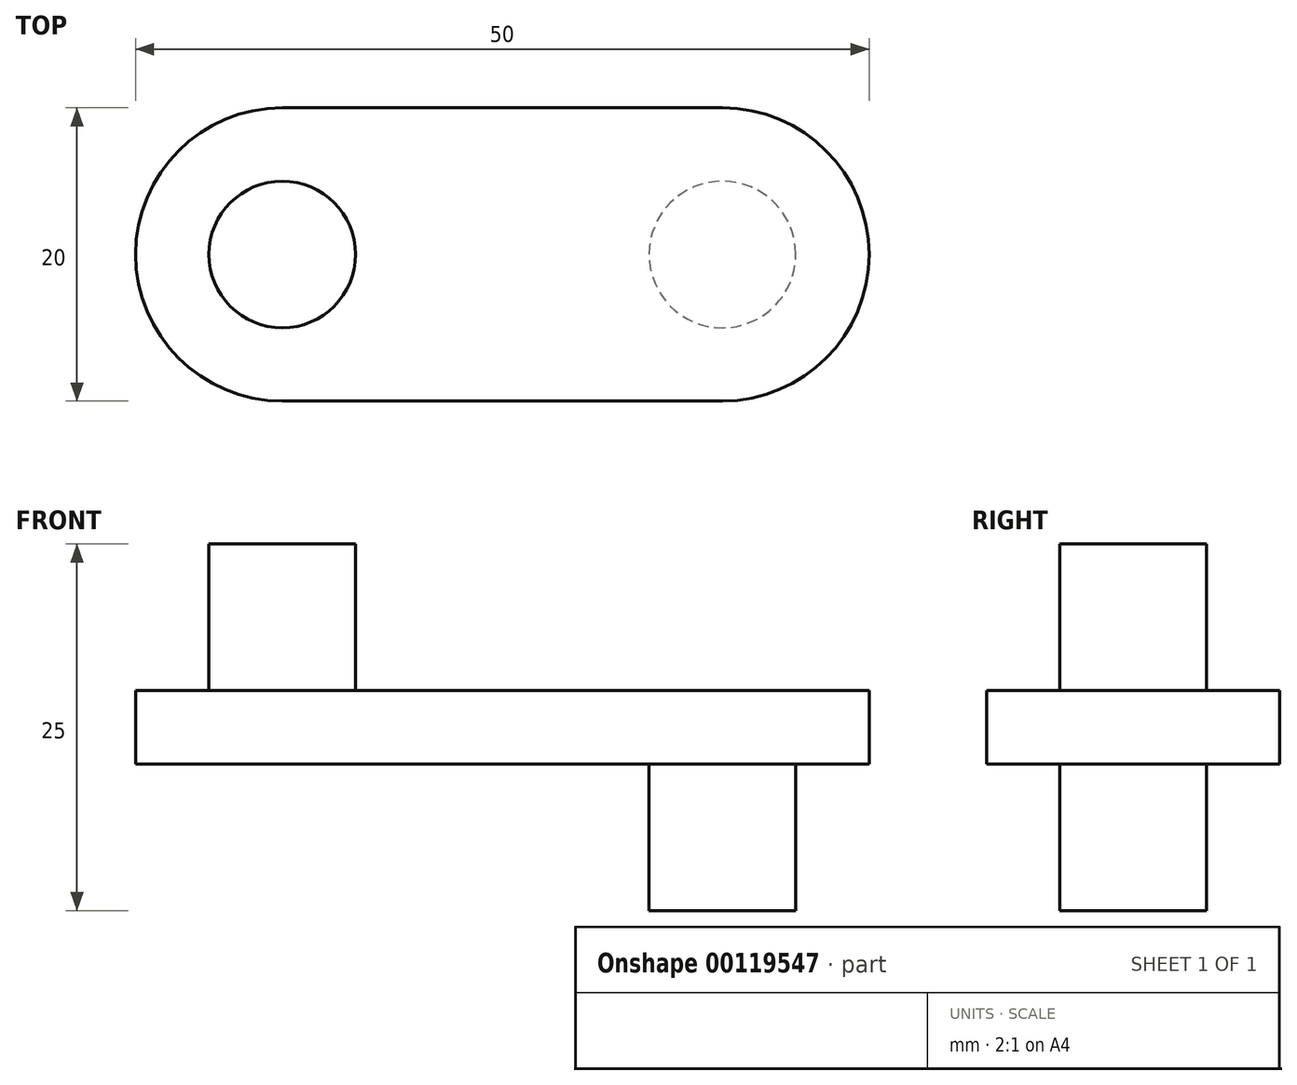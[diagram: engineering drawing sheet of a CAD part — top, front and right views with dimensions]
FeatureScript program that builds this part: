
annotation { "Feature Type Name" : "Feature", "Feature Type Description" : "" }
export const myFeature = defineFeature(function(context is Context, id is Id, definition is map)
    precondition{}
    {
        {
            var Q0;
            Q0=qCreatedBy(makeId("Top.planeOp"),FACE);
            var sketch = newSketch(context, id + "F0", { "sketchPlane" : qUnion([Q0])});
            skLineSegment(sketch, "E0.bottom", {"start": v(0, 0) * mm, "end": v(30, 0) * mm});
            skLineSegment(sketch, "E0.top", {"start": v(0, 20) * mm, "end": v(30, 20) * mm});
            skArc(sketch, "E1", {"start": v(30, 0) * mm, "mid": v(40, 10) * mm, "end": v(30, 20) * mm});
            skArc(sketch, "E2", {"start": v(0, 20) * mm, "mid": v(-10, 10) * mm, "end": v(0, 0) * mm});
            skSolve(sketch);
        }
        {
            var Q0;
            Q0 = qSketchRegion(id + "F0", true);
            extrude(context, id + "F1", {"entities" : qUnion([Q0]), "depth" : 5 * mm});
        }
        {
            var Q0;
            Q0=makeQuery(id+"F1.opExtrude","CAP_FACE",FACE,{"disambiguationData":[OSD([sQuery(id+"F0.wireOp",EDGE,"E0.bottom"),sQuery(id+"F0.wireOp",EDGE,"E0.top"),sQuery(id+"F0.wireOp",EDGE,"E1"),sQuery(id+"F0.wireOp",EDGE,"E2")])],"isStart":false});
            var sketch = newSketch(context, id + "F2", { "sketchPlane" : qUnion([Q0])});
            skLineSegment(sketch, "E3", {"start": v(0, 0) * mm, "end": v(0, 20) * mm, "construction": true});
            skCircle(sketch, "E4", {"center": v(0, 10) * mm, "radius": 5 * mm});
            skSolve(sketch);
        }
        {
            var Q0;
            Q0 = qSketchRegion(id + "F2", true);
            extrude(context, id + "F3", {"entities" : qUnion([Q0]), "operationType" : NewBodyOperationType.ADD, "depth" : 10 * mm});
        }
        {
            var Q0;
            Q0=makeQuery(id+"F1.opExtrude","CAP_FACE",FACE,{"disambiguationData":[OSD([sQuery(id+"F0.wireOp",EDGE,"E0.bottom"),sQuery(id+"F0.wireOp",EDGE,"E0.top"),sQuery(id+"F0.wireOp",EDGE,"E1"),sQuery(id+"F0.wireOp",EDGE,"E2")])],"isStart":true});
            var sketch = newSketch(context, id + "F4", { "sketchPlane" : qUnion([Q0])});
            skLineSegment(sketch, "E5", {"start": v(30, -20) * mm, "end": v(30, 0) * mm, "construction": true});
            skCircle(sketch, "E6", {"center": v(30, -10) * mm, "radius": 5 * mm});
            skSolve(sketch);
        }
        {
            var Q0;
            Q0 = qSketchRegion(id + "F4", true);
            extrude(context, id + "F5", {"entities" : qUnion([Q0]), "operationType" : NewBodyOperationType.ADD, "depth" : 10 * mm});
        }
    });
